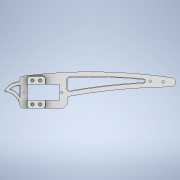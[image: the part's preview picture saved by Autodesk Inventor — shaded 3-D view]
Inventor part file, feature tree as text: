
AUTODESK INVENTOR PART (.ipt)
format: ipt  version: 2020.3 (Build 243373000, 373)  size: 420,864 bytes
history: native  units: mm
features: fillet x9, hole x4, extrude x2, sketch x1, chamfer x1
ambient origin geometry x8: Origin, YZ Plane, XZ Plane, XY Plane, X Axis, Y Axis, Z Axis, Center Point
bodies: Solid1 (feature_tree)
feature tree (17):
  sketch  "Sketch1"  dims[d4=6.0mm d5=24.6mm d6=12.4mm d7=6.0mm d15=7.0mm d17=9.0mm d21=20.0mm d23=80.0mm d24=20.0mm d29=29.670597mm d30=6.0mm d31=10.0mm d33=6.0mm d34=0.0mm d40=3.0mm d41=3.0mm d42=2.0mm d43=4.0mm d44=3.0mm d45=4.0mm d50=13.0mm d51=12.0mm d52=22.68928mm d54=1.9mm d55=50.8mm d56=4.0mm d57=2.0mm d58=90.0deg d59=8.0mm d60=20.594885mm d61=0.5mm d62=2.2mm d63=4.0mm d64=4.0mm d65=2.0mm d66=90.0deg d67=8.0mm d68=20.594885mm d69=20.92mm d70=0.0mm d71=2.0mm d80=3.0mm d81=2.0mm d82=45.0deg d87=0.5mm d88=0.5mm d89=6.8mm d90=28.4mm d99=3.0mm d100=6.0mm d101=4.0mm d102=2.0mm d103=90.0deg d104=4.3mm d105=0.0mm d107=420.0mm d108=4.0mm d109=4.0mm d110=6.0mm d111=2.0mm d112=2.0mm d113=0.5mm d114=2.1mm d115=6.0mm d116=4.0mm d117=2.0mm d118=90.0deg d119=7.3mm d120=0.0mm]
  extrude  "Extrusion1"  Depth=7.3mm
  fillet  "Fillet1"  Radius=12.4mm
  fillet  "Fillet2"  Radius=6.0mm
  fillet  "Fillet3"  Radius=7.0mm
  hole  "Hole1"  [1 undecoded]
  fillet  "Fillet4"  Radius=20.0mm
  hole  "Hole2"  [1 undecoded]
  extrude  "Extrusion3"  Depth=7.3mm
  hole  "Hole5"  [1 undecoded]
  fillet  "Fillet5"  Radius=6.0mm
  chamfer  "Chamfer2"  Distance=10.0mm
  fillet  "Fillet8"  Radius=6.0mm
  fillet  "Fillet10"  Radius=3.0mm
  fillet  "Fillet9"  Radius=3.0mm
  fillet  "Fillet11"  Radius=2.0mm
  hole  "Hole6"  [1 undecoded]
note: 4 required parameter values undecoded (feature->parameter linkage not recoverable at this tier; creation-order binding heuristic only, values carry confidence <= 0.55)
